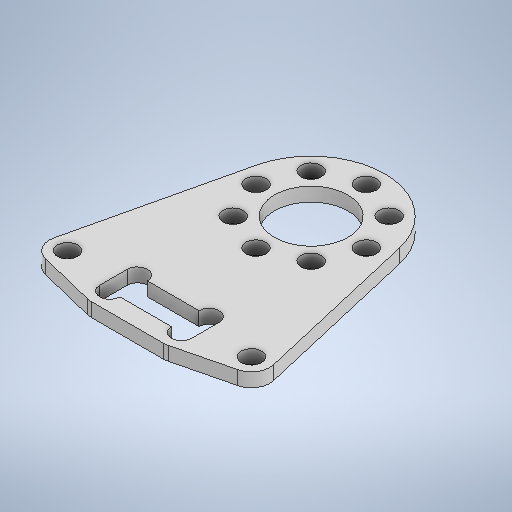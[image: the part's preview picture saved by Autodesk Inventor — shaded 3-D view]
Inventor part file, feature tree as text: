
AUTODESK INVENTOR PART (.ipt)
format: ipt  version: 2025.1 (Build 291241000, 241)  size: 310,272 bytes
history: native  units: mm
features: other x2, extrude x1, sketch x1
ambient origin geometry x8: Origin, YZ Plane, XZ Plane, XY Plane, X Axis, Y Axis, Z Axis, Center Point
bodies: Body1 (feature_tree)
feature tree (4):
  other  "ソリッド1"
  extrude  "押し出し1"  Depth=8.0mm
  sketch  "スケッチ1"
  other  "スケッチ円形状パターン1"
